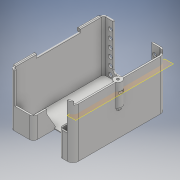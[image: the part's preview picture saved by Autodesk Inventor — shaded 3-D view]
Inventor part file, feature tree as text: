
AUTODESK INVENTOR PART (.ipt)
format: ipt  version: 2018 (Build 220112000, 112)  size: 630,272 bytes
history: native  units: mm
features: reference x23, extrude x15, sketch x15, fillet x13, other x4, plane x2, projected_geometry x2, shell x1
ambient origin geometry x8: Origin, YZ Plane, XZ Plane, XY Plane, X Axis, Y Axis, Z Axis, Center Point
bodies: Solid1 (feature_tree)
feature tree (75):
  extrude  "Extrusion1"  Depth=65.0mm TaperAngle=0.0deg
  sketch  "Sketch2"  dims[d4=2.0mm d6=5.0mm]
  extrude  "Extrusion2"  Depth=5.0mm
  extrude  "Extrusion3"  Depth=2.0mm
  fillet  "Fillet3"  [1 undecoded]
  fillet  "Fillet2"  Radius=100.0mm
  shell  "Shell2"  Thickness=5.0mm
  extrude  "Extrusion4"  Depth=1.321265mm
  extrude  "Extrusion5"  Depth=0.8mm
  extrude  "Extrusion6"  Depth=3.0mm
  extrude  "Extrusion7"  Depth=10.0mm
  fillet  "Fillet4"  Radius=10.0mm
  fillet  "Fillet5"  Radius=100.0mm
  extrude  "Extrusion8"  Depth=2.0mm
  sketch  "Sketch9"  dims[d33=100.0mm d34=0.0mm d35=5.0mm]
  plane  "Work Plane1"
  extrude  "Extrusion9"  Depth=5.0mm
  extrude  "Extrusion10"  Depth=56.0mm
  extrude  "Extrusion11"  Depth=100.0mm TaperAngle=0.0deg
  plane  "Work Plane2"
  extrude  "Extrusion12"  Depth=1.0mm
  extrude  "Extrusion13"  Depth=1.5mm
  extrude  "Extrusion14"  Depth=100.0mm TaperAngle=0.0deg
  fillet  "Fillet15"  Radius=30.0mm
  extrude  "Extrusion15"  Depth=29.0mm TaperAngle=0.0deg
  fillet  "Fillet7"  [1 undecoded]
  fillet  "Fillet9"  Radius=5.7mm
  fillet  "Fillet10"  Radius=10.0mm
  fillet  "Fillet11"  Radius=3.0mm
  fillet  "Fillet13"  Radius=4.0mm
  fillet  "Fillet14"  Radius=3.0mm
  fillet  "Fillet16"  Radius=3.0mm
  fillet  "Fillet17"  Radius=3.0mm
  sketch  "Sketch1"  dims[d0=3.327998mm d1=65.0mm d2=0.0mm]
  reference  "Reference2"
  reference  "Reference3"
  reference  "Reference4"
  reference  "Reference5"
  reference  "Reference6"
  reference  "Reference7"
  reference  "Reference8"
  reference  "Reference9"
  sketch  "Sketch3"  dims[d9=30.0mm d10=0.0mm d11=2.0mm d12=30.0deg d13=100.0mm d14=0.0mm d15=5.0mm]
  reference  "Reference10"
  sketch  "Sketch4"  dims[d16=0.1mm d17=1.321265mm]
  sketch  "Sketch5"  dims[d21=100.0mm d22=0.0mm d23=0.8mm]
  sketch  "Sketch6"  dims[d24=3.0mm d25=3.0mm]
  reference  "Reference11"
  reference  "Reference12"
  reference  "Reference13"
  sketch  "Sketch7"  dims[d26=10.0mm d27=10.0mm d28=10.0mm d29=100.0mm d30=0.0mm]
  sketch  "Sketch8"  dims[d31=7.0mm d32=2.0mm]
  reference  "Reference14"
  reference  "Reference15"
  reference  "Reference16"
  reference  "Reference17"
  sketch  "Sketch10"  dims[d36=80.0mm d38=8.0mm d39=10.0mm d41=10.0mm d43=56.0mm]
  sketch  "Sketch11"  dims[d44=60.0mm d46=10.0mm d47=10.0mm d49=10.0mm d51=100.0mm d52=0.0mm]
  sketch  "Sketch12"  dims[d53=3.0mm d54=1.0mm]
  sketch  "Sketch13"  dims[d55=5.0mm d56=1.5mm]
  reference  "Reference21"
  reference  "Reference22"
  reference  "Reference23"
  sketch  "Sketch14"  dims[d57=100.0mm d58=0.0mm d59=100.0mm d60=0.0mm d62=30.0mm d63=0.0mm]
  sketch  "Sketch15"  dims[d64=3.2mm d65=29.0mm d66=0.0mm d67=-10.0mm d68=5.7mm d69=10.0mm d70=3.0mm d71=0.0mm d72=4.0mm d73=3.0mm d74=0.0mm d75=3.0mm d76=0.0mm d77=3.0mm d78=0.0mm d80=1.0mm d82=1.8mm d83=1.0mm d84=5.0mm d86=10.0mm d87=3.0mm d88=2.0mm d89=2.0mm d90=1.0mm d91=1.0mm]
  reference  "Reference26"
  reference  "Reference28"
  reference  "Reference29"
  projected_geometry  "Projected Loop3"
  projected_geometry  "Projected Loop4"
  reference  "Reference30"
  parser-record x1  (decoder bookkeeping rows leaked as tree rows — omitted from the tree; the rows remain in map.json)
  other  "RAMPS Mount.iam"
  other  "Arduino RAMPS combo:1"
  other  "Mount:1"
note: 2 required parameter values undecoded (feature->parameter linkage not recoverable at this tier; creation-order binding heuristic only, values carry confidence <= 0.55)
note: 1 file-system path scrubbed to <path> (originals preserved in map.json)
